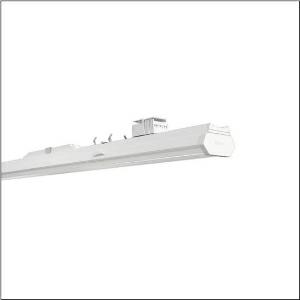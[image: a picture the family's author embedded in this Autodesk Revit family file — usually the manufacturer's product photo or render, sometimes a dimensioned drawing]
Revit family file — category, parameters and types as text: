
# Revit family: licross_r__21_protected_mo_52td12dn4a5g3s_ad63
name_source: partatom
category: Lighting Fixtures
units: mm (PartAtom-declared; Revit-internal decimal feet)

## family parameters
Cut with Voids When Loaded = No
Host = Face
Light Source = No
Part Type = Normal
Room Calculation Point = No
Round Connector Dimension = Use Diameter
Shared = No

## types (1)
- --- (1 x LED, 940 lm, 6.8 W, 4000K)
    Apparent Load = 7 VA
    CIE Flux Codes = 73 92 98 99 100
    Color Rendering = 80
    Color Temperature = 4000K
    Default Elevation = 1800 mm
    Description = Licross® 21 Protected MO, luminaire insert, of sheet steel, galvanised, coil coated, white, length: 1.500mm, width: 90mm, height: 103mm, LED rated luminous flux: 10.700lm, light colour: 840, control gear: DALI 2 (for two DALI lines), with plug, 6-pole, with phase selection, for trunking rail, 14-core, mains connection: 220..240V, AC, 50/60Hz, rated input power: 66W, for trunking rail, 14-core, internal wiring halogen-free, for emergency light function, converter,control gear: single battery element, battery: LiFePO4, 9Ah, primary light control with lens, of plastic, primary optical cover: cover, of PMMA, light emission: direct distribution, primary light characteristic: symmetric, protection rating (complete): IP54, insulation class (complete): insulation class I (protective earthing), certification: CE, UKCA, protection symbol: D if used in an environment with non-conductive dust loads with corresponding accessories, impact resistance: IK06, permissible ambient temperature for indoor applications: +5..+35°C, standard: EN 60598-2-22, LABS conformity tested according to VDMA 24364:2018-05, reducing of maximum allowable ambient temperature of 5°C with ceiling mounting, corresponds to IFS (International Featured Standards) requirements for safety and quality in the food industry, packaging unit: 1 piece
    Height = 92 mm
    Lamp = 1 x LED
    Lamp Light Flux = 940 lm
    Lamp Power = 6.8 W
    Lamp count = 1
    Length = 1500 mm
    Luminous efficacy = 138 lm/W
    Manufacturer = Siteco
    ModVariant = No
    Model = 52TD12DN4A5G3S
    Mounting Place = Ceiling
    Mounting Type = Pendant
    Number of Poles = 1
    OnlyDefault = Yes
    Power Factor = 1
    Product Name = Licross® 21 Protected MO
    Product group = luminaire insert | ceiling pendant
    ProductGroupID = 902
    Protection Class = Protection class I
    Protection Degree = IP 54
    RLX_Detail_Level = 1
    RLX_Emergency_Light_Flux = 0 lm
    RLX_Emergency_Type = 0
    RLX_Emergency_Type_DB = No
    RlxData = <blob elided: 24769 chars, md5=16961d41>
    Socket = socket
    Standby Power = 0 W
    System Light Flux = 940 lm
    System Power = 7 W
    Type Comments = : emergency light operation: 3 h
    Type Image = l_1256148.jpg
    URL = http://relux.com
    VarID = @adj_132413
    Voltage = 0 V
    Weight = 0.00 kg
    Width = 88 mm

## geometry (parser evidence)
native form markers: Blend x4, Sweep x11
no freeform markers — native parametric forms only
